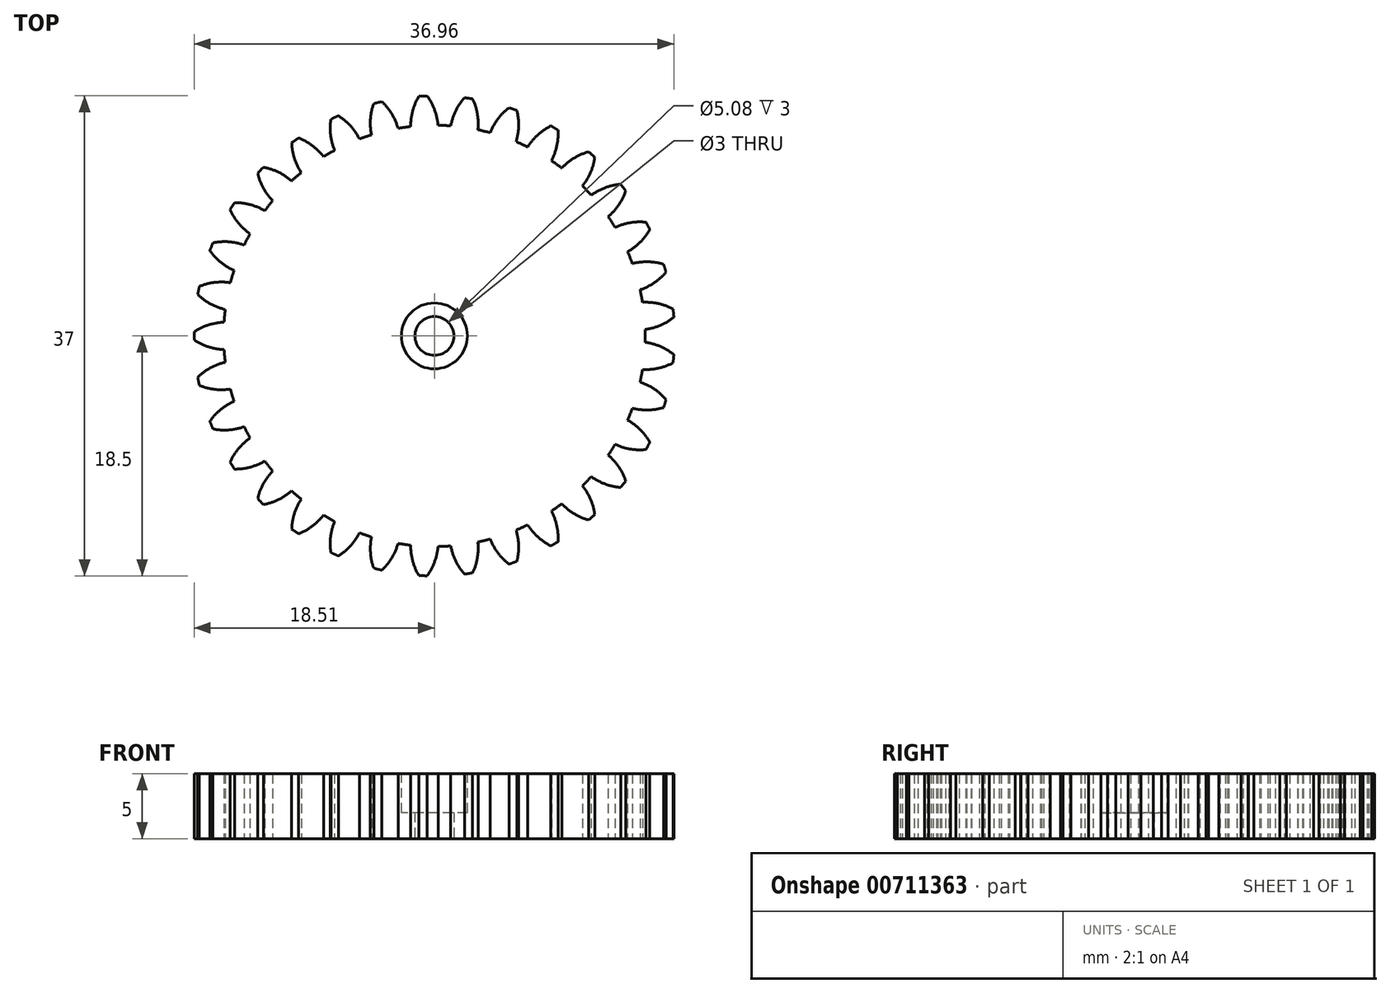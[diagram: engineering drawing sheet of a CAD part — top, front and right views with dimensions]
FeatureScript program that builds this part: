
annotation { "Feature Type Name" : "Feature", "Feature Type Description" : "" }
export const myFeature = defineFeature(function(context is Context, id is Id, definition is map)
    precondition{}
    {
        {
            var Q0;
            Q0=qCreatedBy(makeId("Top.planeOp"),FACE);
            var sketch = newSketch(context, id + "F0", { "sketchPlane" : qUnion([Q0])});
            skCircle(sketch, "E0", {"center": v(0, 0) * mm, "radius": 16.24 * mm});
            skCircle(sketch, "E1", {"center": v(0, 0) * mm, "radius": 17.46 * mm, "construction": true});
            skCircle(sketch, "E2", {"center": v(0, 0) * mm, "radius": 18.52 * mm, "construction": true});
            skLineSegment(sketch, "E3", {"start": v(0, 0) * mm, "end": v(0, 50.63) * mm, "construction": true});
            skLineSegment(sketch, "E4", {"start": v(0, 0) * mm, "end": v(-2.48, 52.12) * mm, "construction": true});
            skLineSegment(sketch, "E5", {"start": v(0, 17.46) * mm, "end": v(-26.32, 17.46) * mm, "construction": true});
            skLineSegment(sketch, "E6", {"start": v(0, 17.46) * mm, "end": v(-24.25, 8.64) * mm, "construction": true});
            skCircle(sketch, "E7", {"center": v(0, 0) * mm, "radius": 16.4 * mm, "construction": true});
            skCircle(sketch, "E8", {"center": v(0, 17.46) * mm, "radius": 4.37 * mm, "construction": true});
            skCircle(sketch, "E9", {"center": v(-4.07, 15.9) * mm, "radius": 4.37 * mm, "construction": true});
            skArc(sketch, "E10", {"start": v(0, 17.46) * mm, "mid": v(-0.25, 18) * mm, "end": v(-0.57, 18.5) * mm});
            skArc(sketch, "E11", {"start": v(0.28, 16.23) * mm, "mid": v(0.18, 16.85) * mm, "end": v(0, 17.46) * mm});
            skCircle(sketch, "E12.MirrorC", {"center": v(2.54, 16.21) * mm, "radius": 4.37 * mm, "construction": true});
            skArc(sketch, "E13.MirrorCS", {"start": v(-1.66, 17.38) * mm, "mid": v(-1.46, 17.94) * mm, "end": v(-1.2, 18.47) * mm});
            skArc(sketch, "E14.MirrorCS", {"start": v(-1.82, 16.13) * mm, "mid": v(-1.79, 16.76) * mm, "end": v(-1.66, 17.38) * mm});
            skArc(sketch, "E15", {"start": v(-0.57, 18.5) * mm, "mid": v(-0.88, 18.48) * mm, "end": v(-1.2, 18.47) * mm});
            skSolve(sketch);
        }
        {
            var Q0;
            {var subQ0=sQuery(id+"F0.wireOp",EDGE,"E0");var subQ1=makeQuery(id+"F0.imprint","INTERSECT",VERTEX,{"derivedFrom":[subQ0,sQuery(id+"F0.wireOp",EDGE,"E11")]});Q0=makeQuery(id+"F0.imprint","IMPRINT",FACE,{"disambiguationData":[TD([[makeQuery(id+"F0.imprint","IMPRINT",EDGE,{"disambiguationData":[TD([[subQ1,-1.0]])],"derivedFrom":subQ0}),1.0]])]});}
            var Q1;
            {var subQ2=sQuery(id+"F0.wireOp",EDGE,"E10");Q1=makeQuery(id+"F0.imprint","IMPRINT",FACE,{"disambiguationData":[TD([[makeQuery(id+"F0.imprint","IMPRINT",EDGE,{"derivedFrom":subQ2}),1.0]])]});}
            extrude(context, id + "F1", {"entities" : qUnion([Q0, Q1]), "depth" : 5 * mm, "offsetDistance" : 25 * mm});
        }
        {
            var Q0;
            Q0=makeQuery(id+"F1.opExtrude","SWEPT_BODY",BODY,{"disambiguationData":[OSD([sQuery(id+"F0.wireOp",EDGE,"E0"),sQuery(id+"F0.wireOp",EDGE,"E10"),sQuery(id+"F0.wireOp",EDGE,"E11"),sQuery(id+"F0.wireOp",EDGE,"E13.MirrorCS"),sQuery(id+"F0.wireOp",EDGE,"E14.MirrorCS"),sQuery(id+"F0.wireOp",EDGE,"E15")])]});
            var Q1;
            Q1=makeQuery(id+"F1.opExtrude","SWEPT_FACE",FACE,{"disambiguationData":[OSD([sQuery(id+"F0.wireOp",EDGE,"E0")])]});
            circularPattern(context, id + "F2", {"entities" : qUnion([Q0]), "axis" : qUnion([Q1]), "angle" : 360 * degree, "instanceCount" : 33, "equalSpace" : true});
        }
        {
            var Q0;
            Q0=makeQuery(id+"F1.opExtrude","CAP_FACE",FACE,{"disambiguationData":[OSD([sQuery(id+"F0.wireOp",EDGE,"E0"),sQuery(id+"F0.wireOp",EDGE,"E10"),sQuery(id+"F0.wireOp",EDGE,"E11"),sQuery(id+"F0.wireOp",EDGE,"E13.MirrorCS"),sQuery(id+"F0.wireOp",EDGE,"E14.MirrorCS"),sQuery(id+"F0.wireOp",EDGE,"E15")])],"isStart":false});
            var sketch = newSketch(context, id + "F3", { "sketchPlane" : qUnion([Q0])});
            skCircle(sketch, "E16", {"center": v(0, 0) * mm, "radius": 2.54 * mm});
            skSolve(sketch);
        }
        {
            var Q0;
            Q0=makeQuery(id+"F3.imprint","IMPRINT",FACE,{"disambiguationData":[TD([[makeQuery(id+"F3.imprint","IMPRINT",EDGE,{"derivedFrom":sQuery(id+"F3.wireOp",EDGE,"E16")}),1.0]])]});
            extrude(context, id + "F4", {"entities" : qUnion([Q0]), "operationType" : NewBodyOperationType.ADD, "depth" : 1 * mm, "offsetDistance" : 25 * mm});
        }
        {
            var Q0;
            Q0=makeQuery(id+"F2.opPattern","COPY",FACE,{"derivedFrom":makeQuery(id+"F1.opExtrude","CAP_FACE",FACE,{"disambiguationData":[OSD([sQuery(id+"F0.wireOp",EDGE,"E0"),sQuery(id+"F0.wireOp",EDGE,"E10"),sQuery(id+"F0.wireOp",EDGE,"E11"),sQuery(id+"F0.wireOp",EDGE,"E13.MirrorCS"),sQuery(id+"F0.wireOp",EDGE,"E14.MirrorCS"),sQuery(id+"F0.wireOp",EDGE,"E15")])],"isStart":true}),"instanceName":"3"});
            var sketch = newSketch(context, id + "F5", { "sketchPlane" : qUnion([Q0])});
            skCircle(sketch, "E17", {"center": v(0, 0) * mm, "radius": 1.5 * mm});
            skSolve(sketch);
        }
        {
            var Q0;
            Q0=makeQuery(id+"F5.imprint","IMPRINT",FACE,{"disambiguationData":[TD([[makeQuery(id+"F5.imprint","IMPRINT",EDGE,{"derivedFrom":sQuery(id+"F5.wireOp",EDGE,"E17")}),1.0]])]});
            extrude(context, id + "F6", {"entities" : qUnion([Q0]), "operationType" : NewBodyOperationType.ADD, "depth" : 1 * mm, "offsetDistance" : 25 * mm});
        }
        {
            var Q0;
            Q0=makeQuery(id+"F4.opExtrude","CAP_FACE",FACE,{"disambiguationData":[OSD([sQuery(id+"F3.wireOp",EDGE,"E16")])],"isStart":false});
            var sketch = newSketch(context, id + "F7", { "sketchPlane" : qUnion([Q0])});
            skCircle(sketch, "E18", {"center": v(0, 0) * mm, "radius": 2.54 * mm});
            skSolve(sketch);
        }
        {
            var Q0;
            Q0=makeQuery(id+"F7.imprint","IMPRINT",FACE,{"disambiguationData":[TD([[makeQuery(id+"F7.imprint","IMPRINT",EDGE,{"derivedFrom":sQuery(id+"F7.wireOp",EDGE,"E18")}),1.0]])]});
            extrude(context, id + "F8", {"entities" : qUnion([Q0]), "operationType" : NewBodyOperationType.REMOVE, "oppositeDirection" : true, "depth" : 4 * mm, "offsetDistance" : 25 * mm});
        }
        {
            var Q0;
            Q0=makeQuery(id+"F6.opExtrude","CAP_FACE",FACE,{"disambiguationData":[OSD([sQuery(id+"F5.wireOp",EDGE,"E17")])],"isStart":false});
            var sketch = newSketch(context, id + "F9", { "sketchPlane" : qUnion([Q0])});
            skCircle(sketch, "E19", {"center": v(0, 0) * mm, "radius": 1.5 * mm});
            skSolve(sketch);
        }
        {
            var Q0;
            Q0=makeQuery(id+"F9.imprint","IMPRINT",FACE,{"disambiguationData":[TD([[makeQuery(id+"F9.imprint","IMPRINT",EDGE,{"derivedFrom":sQuery(id+"F9.wireOp",EDGE,"E19")}),1.0]])]});
            extrude(context, id + "F10", {"entities" : qUnion([Q0]), "operationType" : NewBodyOperationType.REMOVE, "oppositeDirection" : true, "depth" : 8 * mm, "offsetDistance" : 25 * mm});
        }
    });
